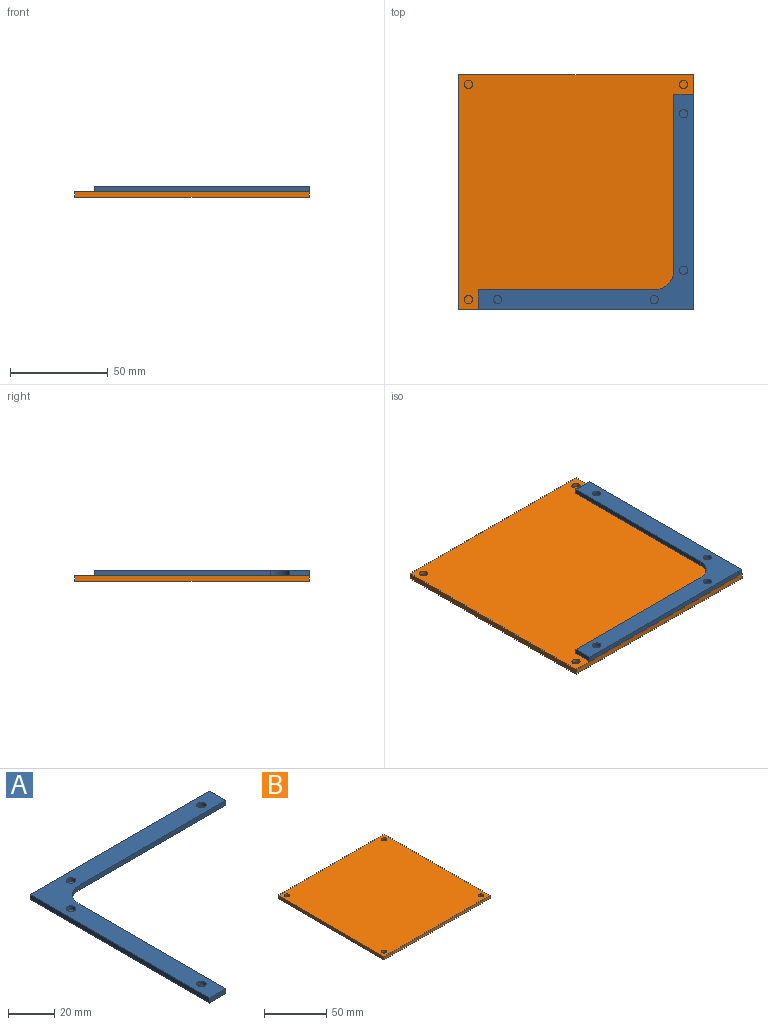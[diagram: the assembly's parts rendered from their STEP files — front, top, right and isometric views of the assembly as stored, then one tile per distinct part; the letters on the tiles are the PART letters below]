
ASSEMBLY  parts=2 mates=1
PART A: 17 faces, bbox 110x110x2.6 mm
  f0: plane 110x2.6mm, normal (-1,0,0), area 286mm2, adj f1,f6,f7,f8
  f1: plane 10x2.6mm, normal (0,-1,0), area 26mm2, adj f0,f2,f7,f8
  f2: plane 90x2.6mm, normal (1,0,0), area 234mm2, adj f1,f3,f7,f8
  f3: cylinder r=10mm len=10mm, axis (0,0,-1), area 40.8mm2, adj f2,f4,f7,f8
  f4: plane 90x2.6mm, normal (0,-1,0), area 234mm2, adj f3,f5,f7,f8
  f5: plane 10x2.6mm, normal (1,0,0), area 26mm2, adj f4,f6,f7,f8
  f6: plane 110x2.6mm, normal (0,1,0), area 286mm2, adj f0,f5,f7,f8
  f7: plane 110x110mm, normal (0,0,1), area 2066mm2, adj f0,f1,f2,f3,f4,f5,f6,f9
  f8: plane 110x110mm, normal (0,0,-1), area 2121.5mm2, adj f0,f1,f2,f3,f4,f5,f6
  f9: cylinder r=2.1mm len=4.2mm, axis (0,0,1), area 26.4mm2, adj f7,f10
  f10: plane 4.2x4.2mm, normal (0,0,1), area 13.9mm2, adj f9
  f11: cylinder r=2.1mm len=4.2mm, axis (0,0,1), area 26.4mm2, adj f7,f12
  f12: plane 4.2x4.2mm, normal (0,0,1), area 13.9mm2, adj f11
  f13: cylinder r=2.1mm len=4.2mm, axis (0,0,1), area 26.4mm2, adj f7,f14
  f14: plane 4.2x4.2mm, normal (0,0,1), area 13.9mm2, adj f13
  f15: cylinder r=2.1mm len=4.2mm, axis (0,0,1), area 26.4mm2, adj f7,f16
  f16: plane 4.2x4.2mm, normal (0,0,1), area 13.9mm2, adj f15
PART B: 14 faces, bbox 120x120x3 mm
  f0: plane 120x3mm, normal (0,1,0), area 360mm2, adj f1,f3,f4,f5
  f1: plane 120x3mm, normal (-1,0,0), area 360mm2, adj f0,f2,f4,f5
  f2: plane 120x3mm, normal (0,-1,0), area 360mm2, adj f1,f3,f4,f5
  f3: plane 120x3mm, normal (1,0,0), area 360mm2, adj f0,f2,f4,f5
  f4: plane 120x120mm, normal (0,0,1), area 14344.6mm2, adj f0,f1,f2,f3,f6,f8,f10,f12
  f5: plane 120x120mm, normal (0,0,-1), area 14400mm2, adj f0,f1,f2,f3
  f6: cylinder r=2.1mm len=4.2mm, axis (0,0,1), area 26.4mm2, adj f4,f7
  f7: plane 4.2x4.2mm, normal (0,0,1), area 13.9mm2, adj f6
  f8: cylinder r=2.1mm len=4.2mm, axis (0,0,1), area 26.4mm2, adj f4,f9
  f9: plane 4.2x4.2mm, normal (0,0,1), area 13.9mm2, adj f8
  f10: cylinder r=2.1mm len=4.2mm, axis (0,0,1), area 26.4mm2, adj f4,f11
  f11: plane 4.2x4.2mm, normal (0,0,1), area 13.9mm2, adj f10
  f12: cylinder r=2.1mm len=4.2mm, axis (0,0,1), area 26.4mm2, adj f4,f13
  f13: plane 4.2x4.2mm, normal (0,0,1), area 13.9mm2, adj f12
PLACE A rot(axis=(0,0,1),180deg) t=(18.34,-21.68,0.54)mm
PLACE B t=(-36.66,-21.68,-0.96)mm
MATE fastened A.f8 <-> B.f4  axis (0,0,1) through (23.34,-81.68,0.54)mm
